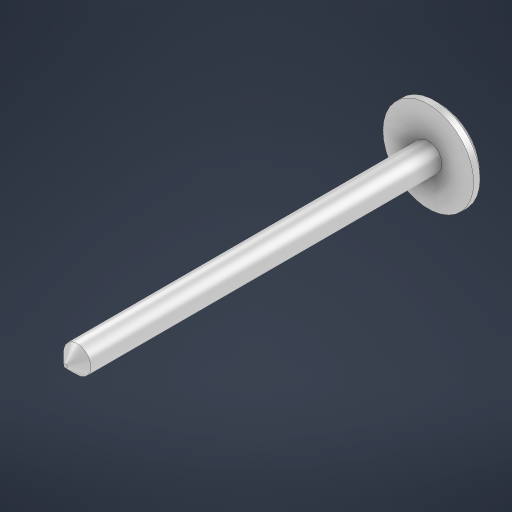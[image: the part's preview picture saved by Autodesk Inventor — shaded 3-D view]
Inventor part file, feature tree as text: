
AUTODESK INVENTOR PART (.ipt)
format: ipt  version: 2023 (Build 270158000, 158)  size: 289,792 bytes
history: native  units: mm
features: chamfer x5, extrude x3, sketch x3, fillet x1
ambient origin geometry x8: Origin, YZ Plane, XZ Plane, XY Plane, X Axis, Y Axis, Z Axis, Center Point
bodies: Solid1 (feature_tree)
feature tree (12):
  extrude  "Extrusion1"  Depth=2.0mm TaperAngle=0.0deg
  extrude  "Extrusion2"  Depth=40.0mm TaperAngle=0.0deg
  chamfer  "Chamfer1"  Distance=1.3mm Angle=45.0deg
  chamfer  "Chamfer2"  Distance=1.3mm Angle=45.0deg
  fillet  "Fillet1"  Radius=3.0mm
  extrude  "Extrusion3"  Depth=1.0mm
  chamfer  "Chamfer3"  Distance=1.0mm
  chamfer  "Chamfer4"  Distance=0.5mm Angle=45.0deg
  chamfer  "Chamfer5"  Distance=0.5mm Angle=45.0deg
  sketch  "Sketch1"  dims[d0=10.0mm d1=2.0mm d2=0.0mm]
  sketch  "Sketch2"  dims[d3=3.0mm d4=40.0mm d5=0.0mm d6=1.3mm d7=2.0mm d8=45.0deg d9=1.3mm d10=2.0mm d11=45.0deg d12=3.0mm]
  sketch  "Sketch3"  dims[d15=6.0mm d16=1.0mm d17=1.0mm d18=0.0mm d19=0.5mm d20=2.0mm d21=45.0deg d22=0.5mm d23=2.0mm d24=45.0deg d25=0.5mm d26=2.0mm d27=45.0deg]
